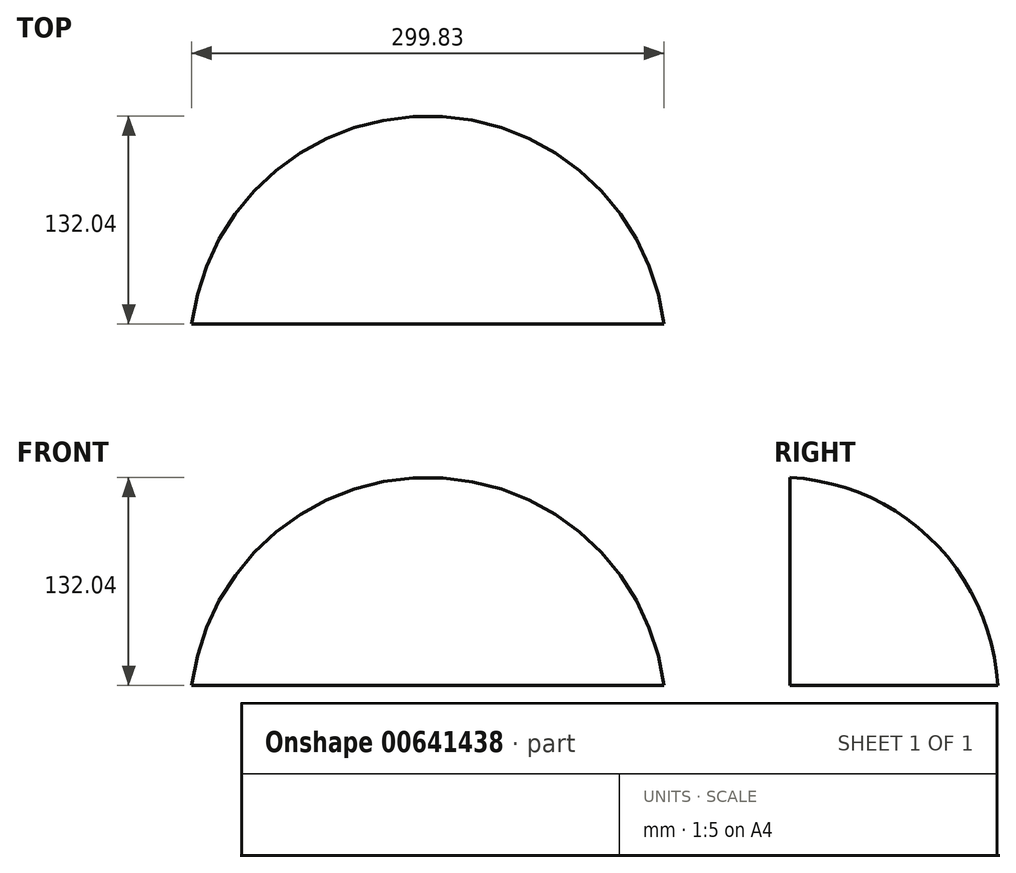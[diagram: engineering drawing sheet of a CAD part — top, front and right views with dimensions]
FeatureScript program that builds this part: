
annotation { "Feature Type Name" : "Feature", "Feature Type Description" : "" }
export const myFeature = defineFeature(function(context is Context, id is Id, definition is map)
    precondition{}
    {
        {
            var Q0;
            Q0=qCreatedBy(makeId("Front.planeOp"),FACE);
            var sketch = newSketch(context, id + "F0", { "sketchPlane" : qUnion([Q0])});
            skArc(sketch, "E0", {"start": v(143.42, 0) * mm, "mid": v(-7.64, 132.24) * mm, "end": v(-158.7, 0) * mm});
            skLineSegment(sketch, "E1", {"start": v(-158.7, 0) * mm, "end": v(143.42, 0) * mm});
            skSolve(sketch);
        }
        {
            var Q0;
            Q0 = qSketchRegion(id + "F0", true);
            extrude(context, id + "F1", {"entities" : qUnion([Q0]), "oppositeDirection" : true, "depth" : 152.4 * mm, "offsetDistance" : 25.4 * mm});
        }
        {
            var Q0;
            Q0=makeQuery(id+"F1.opExtrude","SWEPT_FACE",FACE,{"disambiguationData":[OSD([sQuery(id+"F0.wireOp",EDGE,"E1")])]});
            var sketch = newSketch(context, id + "F2", { "sketchPlane" : qUnion([Q0])});
            skArc(sketch, "E2", {"start": v(-158.7, 0) * mm, "mid": v(-7.64, -132.24) * mm, "end": v(143.42, 0) * mm});
            skSolve(sketch);
        }
        {
            var Q0;
            Q0=makeQuery(id+"F2.imprint","IMPRINT",FACE,{"disambiguationData":[TD([[makeQuery(id+"F2.imprint","IMPRINT",EDGE,{"derivedFrom":sQuery(id+"F2.wireOp",EDGE,"E2")}),-1.0]])]});
            extrude(context, id + "F3", {"entities" : qUnion([Q0]), "operationType" : NewBodyOperationType.REMOVE, "oppositeDirection" : true, "depth" : 152.4 * mm, "offsetDistance" : 25.4 * mm});
        }
        {
            var Q0;
            Q0=makeQuery(id+"F3.boolean.opBoolean","INTERSECT",EDGE,{"derivedFrom":[makeQuery(id+"F1.opExtrude","SWEPT_FACE",FACE,{"disambiguationData":[OSD([sQuery(id+"F0.wireOp",EDGE,"E0")])]}),makeQuery(id+"F3.opExtrude","SWEPT_FACE",FACE,{"disambiguationData":[OSD([sQuery(id+"F2.wireOp",EDGE,"E2")])]})]});
            fillet(context, id + "F4", {"entities" : qUnion([Q0]), "radius" : 139.7 * mm, "tangentPropagation" : true, "allowEdgeOverflow" : false});
        }
    });
